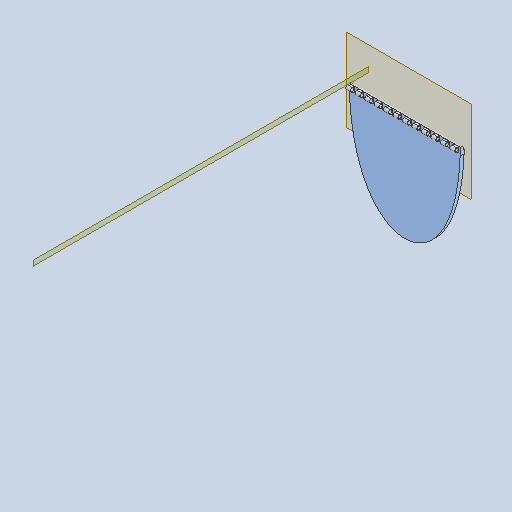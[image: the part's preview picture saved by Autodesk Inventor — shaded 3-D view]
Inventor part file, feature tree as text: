
AUTODESK INVENTOR PART (.ipt)
format: ipt  version: 2023 (Build 270158030, 158C)  size: 172,544 bytes
history: native  units: mm
features: other x4, plane x2, extrude x2, sketch x2, fillet x1, pattern_linear x1, reference x1
ambient origin geometry x8: Origin, YZ Plane, XZ Plane, XY Plane, X Axis, Y Axis, Z Axis, Center Point
bodies: Body1 (feature_tree)
feature tree (13):
  other  "back-flap"
  plane  "Work Plane1"
  extrude  "Extrusion1"  Depth=850.0mm
  plane  "Work Plane2"
  extrude  "Extrusion2"  Depth=30.0mm
  fillet  "Fillet1"  Radius=30.0mm
  pattern_linear  "Rectangular Pattern1"  Count1=35  [1 undecoded]
  sketch  "Sketch1"  dims[d0=50.0mm d1=850.0mm]
  reference  "Reference1"
  sketch  "Sketch3"  dims[d2=700.0mm d3=30.0mm d4=30.0mm d5=350.0mm d6=350.0mm d7=25.0mm d8=0.0mm d11=12.5mm d12=2.5mm d13=20.0mm d14=10.0mm d15=3.0mm d16=25.0mm d17=14.0mm d18=12.5mm d19=30.0mm d20=0.0mm d21=25.0mm d22=120.0mm d24=60.0mm]
  other  "<userpath>\Documents\0004-inventor\3D-CAD-main\primary-engineer-bench.iam"
  other  "primary-engineer-bench.iam"
  other  "bed-base:1"
note: 1 required parameter value undecoded (feature->parameter linkage not recoverable at this tier; creation-order binding heuristic only, values carry confidence <= 0.55)
